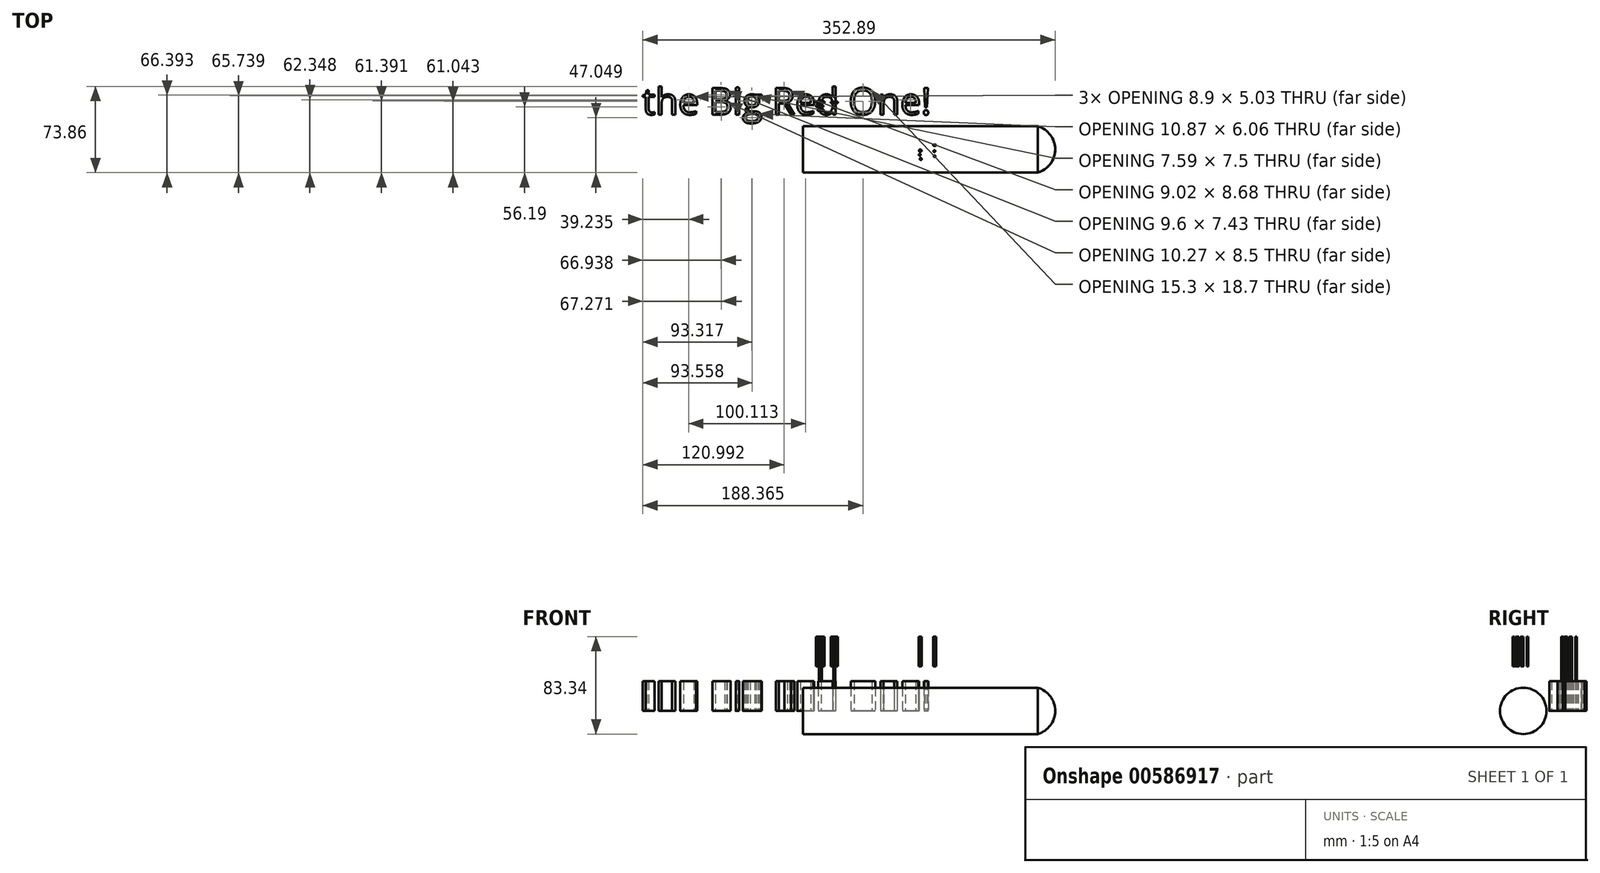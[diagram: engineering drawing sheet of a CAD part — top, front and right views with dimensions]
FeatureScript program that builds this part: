
annotation { "Feature Type Name" : "Feature", "Feature Type Description" : "" }
export const myFeature = defineFeature(function(context is Context, id is Id, definition is map)
    precondition{}
    {
        {
            var Q0;
            Q0=qCreatedBy(makeId("Top.planeOp"),FACE);
            var sketch = newSketch(context, id + "F0", { "sketchPlane" : qUnion([Q0])});
            skLineSegment(sketch, "E0.bottom", {"start": v(-109.4, 0) * mm, "end": v(86.66, 0) * mm});
            skLineSegment(sketch, "E0.top", {"start": v(-109.4, 19.84) * mm, "end": v(106.5, 19.84) * mm});
            skLineSegment(sketch, "E0.left", {"start": v(-109.4, 0) * mm, "end": v(-109.4, 19.84) * mm});
            skLineSegment(sketch, "E0.right", {"start": v(106.5, 0) * mm, "end": v(106.5, 19.84) * mm});
            skArc(sketch, "E1", {"start": v(106.5, 0) * mm, "mid": v(102.35, 12.42) * mm, "end": v(91.57, 19.84) * mm});
            skLineSegment(sketch, "E2", {"start": v(86.66, 0) * mm, "end": v(106.5, 0) * mm});
            skSolve(sketch);
        }
        {
            var Q0;
            Q0=makeQuery(id+"F0.imprint","IMPRINT",FACE,{"disambiguationData":[TD([[makeQuery(id+"F0.imprint","IMPRINT",EDGE,{"derivedFrom":sQuery(id+"F0.wireOp",EDGE,"E0.bottom")}),1.0]])]});
            var Q1;
            Q1=sQuery(id+"F0.wireOp",EDGE,"E2");
            revolve(context, id + "F1", {"entities" : qUnion([Q0]), "axis" : qUnion([Q1]), "revolveType" : RevolveType.FULL});
        }
        {
            var Q0;
            Q0=qCreatedBy(makeId("Top.planeOp"),FACE);
            var sketch = newSketch(context, id + "F2", { "sketchPlane" : qUnion([Q0])});
            skText(sketch, "E3", { "text": "the Big Red One!", "fontName": "OpenSans-Regular.ttf"});
            const initialGuessF2  = {"E3": [-0.24686, 0.02985, 1, 0, 0.0229]};
            skSetInitialGuess(sketch, initialGuessF2);
            skSolve(sketch);
        }
        {
            var Q0;
            Q0 = qSketchRegion(id + "F2", true);
            extrude(context, id + "F3", {"entities" : qUnion([Q0]), "depth" : 25.4 * mm, "offsetDistance" : 25.4 * mm});
        }
        {
            var Q0;
            Q0=makeQuery(id+"F3.opExtrude","CAP_FACE",FACE,{"disambiguationData":[OSD([sQuery(id+"F2.wireOp",EDGE,"E3.sketch_text.stroke-174"),sQuery(id+"F2.wireOp",EDGE,"E3.sketch_text.stroke-175"),sQuery(id+"F2.wireOp",EDGE,"E3.sketch_text.stroke-176"),sQuery(id+"F2.wireOp",EDGE,"E3.sketch_text.stroke-177"),sQuery(id+"F2.wireOp",EDGE,"E3.sketch_text.stroke-178"),sQuery(id+"F2.wireOp",EDGE,"E3.sketch_text.stroke-179"),sQuery(id+"F2.wireOp",EDGE,"E3.sketch_text.stroke-180"),sQuery(id+"F2.wireOp",EDGE,"E3.sketch_text.stroke-181"),sQuery(id+"F2.wireOp",EDGE,"E3.sketch_text.stroke-182"),sQuery(id+"F2.wireOp",EDGE,"E3.sketch_text.stroke-183"),sQuery(id+"F2.wireOp",EDGE,"E3.sketch_text.stroke-184"),sQuery(id+"F2.wireOp",EDGE,"E3.sketch_text.stroke-185"),sQuery(id+"F2.wireOp",EDGE,"E3.sketch_text.stroke-186"),sQuery(id+"F2.wireOp",EDGE,"E3.sketch_text.stroke-187"),sQuery(id+"F2.wireOp",EDGE,"E3.sketch_text.stroke-188"),sQuery(id+"F2.wireOp",EDGE,"E3.sketch_text.stroke-189"),sQuery(id+"F2.wireOp",EDGE,"E3.sketch_text.stroke-190"),sQuery(id+"F2.wireOp",EDGE,"E3.sketch_text.stroke-191"),sQuery(id+"F2.wireOp",EDGE,"E3.sketch_text.stroke-192"),sQuery(id+"F2.wireOp",EDGE,"E3.sketch_text.stroke-193"),sQuery(id+"F2.wireOp",EDGE,"E3.sketch_text.stroke-194"),sQuery(id+"F2.wireOp",EDGE,"E3.sketch_text.stroke-195"),sQuery(id+"F2.wireOp",EDGE,"E3.sketch_text.stroke-196"),sQuery(id+"F2.wireOp",EDGE,"E3.sketch_text.stroke-197")])],"isStart":false});
            var sketch = newSketch(context, id + "F4", { "sketchPlane" : qUnion([Q0])});
            skCircle(sketch, "E4", {"center": v(-94.54, 40.59) * mm, "radius": 1.11 * mm});
            skCircle(sketch, "E5", {"center": v(-94.99, 37.08) * mm, "radius": 0.76 * mm});
            skCircle(sketch, "E6", {"center": v(-94.08, 33.43) * mm, "radius": 0.85 * mm});
            skCircle(sketch, "E7", {"center": v(-82.21, 45.23) * mm, "radius": 0.56 * mm});
            skCircle(sketch, "E8", {"center": v(-82.5, 40.18) * mm, "radius": 0.75 * mm});
            skCircle(sketch, "E9", {"center": v(-82.37, 35.93) * mm, "radius": 0.67 * mm});
            skSolve(sketch);
        }
        {
            var Q0;
            Q0 = qSketchRegion(id + "F4", true);
            extrude(context, id + "F5", {"entities" : qUnion([Q0]), "operationType" : NewBodyOperationType.ADD, "depth" : 12.7 * mm, "offsetDistance" : 25.4 * mm});
        }
        {
            var Q0;
            Q0=makeQuery(id+"F5.opExtrude","CAP_FACE",FACE,{"disambiguationData":[OSD([sQuery(id+"F4.wireOp",EDGE,"E6")])],"isStart":false});
            var sketch = newSketch(context, id + "F6", { "sketchPlane" : qUnion([Q0])});
            skCircle(sketch, "E10.0", {"center": v(-94.08, 33.43) * mm, "radius": 0.85 * mm});
            skCircle(sketch, "E11.0.0", {"center": v(-94.99, 37.08) * mm, "radius": 0.76 * mm});
            skCircle(sketch, "E12.0.0", {"center": v(-94.54, 40.59) * mm, "radius": 1.11 * mm});
            skCircle(sketch, "E13.0", {"center": v(-82.37, 35.93) * mm, "radius": 0.67 * mm});
            skCircle(sketch, "E14.0", {"center": v(-82.5, 40.18) * mm, "radius": 0.75 * mm});
            skCircle(sketch, "E15.0", {"center": v(-82.21, 45.23) * mm, "radius": 0.56 * mm});
            skLineSegment(sketch, "E16.bottom", {"start": v(-80.97, 44.83) * mm, "end": v(-83.45, 44.83) * mm});
            skLineSegment(sketch, "E16.top", {"start": v(-80.97, 45.64) * mm, "end": v(-83.45, 45.64) * mm});
            skLineSegment(sketch, "E16.left", {"start": v(-80.97, 44.83) * mm, "end": v(-80.97, 45.64) * mm});
            skLineSegment(sketch, "E16.right", {"start": v(-83.45, 44.83) * mm, "end": v(-83.45, 45.64) * mm});
            skCircle(sketch, "E17.0", {"center": v(-8.47, -8.26) * mm, "radius": 0.85 * mm});
            skCircle(sketch, "E18.0.0", {"center": v(-9.37, -4.61) * mm, "radius": 0.76 * mm});
            skCircle(sketch, "E19.0.0", {"center": v(-8.93, -1.1) * mm, "radius": 1.11 * mm});
            skCircle(sketch, "E20.0", {"center": v(3.25, -5.76) * mm, "radius": 0.67 * mm});
            skCircle(sketch, "E21.0", {"center": v(3.11, -1.5) * mm, "radius": 0.75 * mm});
            skCircle(sketch, "E22.0", {"center": v(3.4, 3.54) * mm, "radius": 0.56 * mm});
            skLineSegment(sketch, "E23.bottom", {"start": v(4.64, 3.14) * mm, "end": v(2.16, 3.14) * mm});
            skLineSegment(sketch, "E23.top", {"start": v(4.64, 3.95) * mm, "end": v(2.16, 3.95) * mm});
            skLineSegment(sketch, "E23.left", {"start": v(4.64, 3.14) * mm, "end": v(4.64, 3.95) * mm});
            skLineSegment(sketch, "E23.right", {"start": v(2.16, 3.14) * mm, "end": v(2.16, 3.95) * mm});
            skLineSegment(sketch, "E24.bottom", {"start": v(-79.6, 40.76) * mm, "end": v(-85.4, 40.76) * mm});
            skLineSegment(sketch, "E24.top", {"start": v(-79.6, 39.6) * mm, "end": v(-85.4, 39.6) * mm});
            skLineSegment(sketch, "E24.left", {"start": v(-79.6, 40.76) * mm, "end": v(-79.6, 39.6) * mm});
            skLineSegment(sketch, "E24.right", {"start": v(-85.4, 40.76) * mm, "end": v(-85.4, 39.6) * mm});
            skLineSegment(sketch, "E25.bottom", {"start": v(-80.97, 36.5) * mm, "end": v(-83.77, 36.5) * mm});
            skLineSegment(sketch, "E25.top", {"start": v(-80.97, 35.36) * mm, "end": v(-83.77, 35.36) * mm});
            skLineSegment(sketch, "E25.left", {"start": v(-80.97, 36.5) * mm, "end": v(-80.97, 35.36) * mm});
            skLineSegment(sketch, "E25.right", {"start": v(-83.77, 36.5) * mm, "end": v(-83.77, 35.36) * mm});
            skLineSegment(sketch, "E26.bottom", {"start": v(-90.9, 41.3) * mm, "end": v(-98.17, 41.3) * mm});
            skLineSegment(sketch, "E26.top", {"start": v(-90.9, 39.88) * mm, "end": v(-98.17, 39.88) * mm});
            skLineSegment(sketch, "E26.left", {"start": v(-90.9, 41.3) * mm, "end": v(-90.9, 39.88) * mm});
            skLineSegment(sketch, "E26.right", {"start": v(-98.17, 41.3) * mm, "end": v(-98.17, 39.88) * mm});
            skLineSegment(sketch, "E27.bottom", {"start": v(-91.83, 37.77) * mm, "end": v(-98.14, 37.77) * mm});
            skLineSegment(sketch, "E27.top", {"start": v(-91.83, 36.38) * mm, "end": v(-98.14, 36.38) * mm});
            skLineSegment(sketch, "E27.left", {"start": v(-91.83, 37.77) * mm, "end": v(-91.83, 36.38) * mm});
            skLineSegment(sketch, "E27.right", {"start": v(-98.14, 37.77) * mm, "end": v(-98.14, 36.38) * mm});
            skLineSegment(sketch, "E28.bottom", {"start": v(-91.65, 34.07) * mm, "end": v(-96.51, 34.07) * mm});
            skLineSegment(sketch, "E28.top", {"start": v(-91.65, 32.78) * mm, "end": v(-96.51, 32.78) * mm});
            skLineSegment(sketch, "E28.left", {"start": v(-91.65, 34.07) * mm, "end": v(-91.65, 32.78) * mm});
            skLineSegment(sketch, "E28.right", {"start": v(-96.51, 34.07) * mm, "end": v(-96.51, 32.78) * mm});
            skSolve(sketch);
        }
        {
            var Q0;
            Q0 = qSketchRegion(id + "F6", true);
            extrude(context, id + "F7", {"entities" : qUnion([Q0]), "operationType" : NewBodyOperationType.ADD, "depth" : 25.4 * mm, "offsetDistance" : 25.4 * mm});
        }
    });
